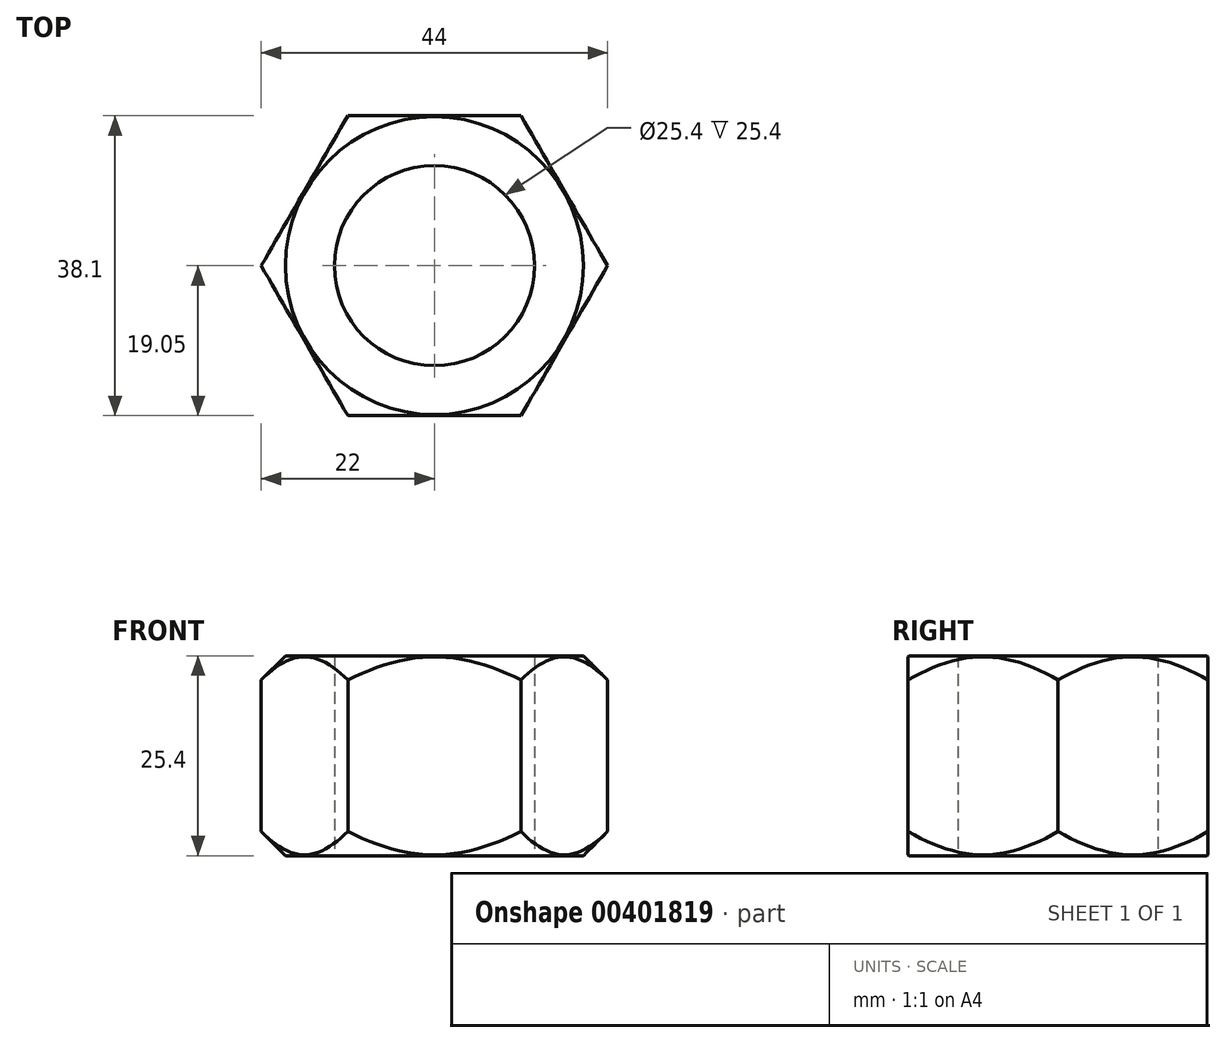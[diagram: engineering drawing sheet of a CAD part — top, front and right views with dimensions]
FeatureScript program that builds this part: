
annotation { "Feature Type Name" : "Feature", "Feature Type Description" : "" }
export const myFeature = defineFeature(function(context is Context, id is Id, definition is map)
    precondition{}
    {
        {
            var Q0;
            Q0=qCreatedBy(makeId("Top.planeOp"),FACE);
            var sketch = newSketch(context, id + "F0", { "sketchPlane" : qUnion([Q0])});
            skCircle(sketch, "E0.cCircle", {"center": v(0, 0) * mm, "radius": 19.05 * mm, "construction": true});
            skLineSegment(sketch, "E0.0", {"start": v(-11, 19.05) * mm, "end": v(11, 19.05) * mm});
            skLineSegment(sketch, "E0.1", {"start": v(11, 19.05) * mm, "end": v(22, 0) * mm});
            skLineSegment(sketch, "E0.2", {"start": v(22, 0) * mm, "end": v(11, -19.05) * mm});
            skLineSegment(sketch, "E0.3", {"start": v(11, -19.05) * mm, "end": v(-11, -19.05) * mm});
            skLineSegment(sketch, "E0.4", {"start": v(-11, -19.05) * mm, "end": v(-22, 0) * mm});
            skLineSegment(sketch, "E0.5", {"start": v(-22, 0) * mm, "end": v(-11, 19.05) * mm});
            skPoint(sketch, "E0.0.midPoint", {"position": v(0, 19.05) * mm});
            skCircle(sketch, "E1", {"center": v(0, 0) * mm, "radius": 12.7 * mm});
            skSolve(sketch);
        }
        {
            var Q0;
            Q0=makeQuery(id+"F0.imprint","IMPRINT",FACE,{"disambiguationData":[TD([[makeQuery(id+"F0.imprint","IMPRINT",EDGE,{"derivedFrom":sQuery(id+"F0.wireOp",EDGE,"E0.0")}),-1.0]])]});
            extrude(context, id + "F1", {"entities" : qUnion([Q0]), "depth" : 25.4 * mm});
        }
        {
            var Q0;
            Q0=qCreatedBy(makeId("Front.planeOp"),FACE);
            var sketch = newSketch(context, id + "F2", { "sketchPlane" : qUnion([Q0])});
            skLineSegment(sketch, "E2.bottom", {"start": v(-18.92, 0) * mm, "end": v(-22.1, 0) * mm});
            skLineSegment(sketch, "E2.top", {"start": v(-18.92, 25.4) * mm, "end": v(-22.1, 25.4) * mm});
            skLineSegment(sketch, "E2.right", {"start": v(-22.1, 0) * mm, "end": v(-22.1, 3.17) * mm});
            skLineSegment(sketch, "E3", {"start": v(-22.1, 3.18) * mm, "end": v(-18.92, 0) * mm});
            skLineSegment(sketch, "E4", {"start": v(-22.1, 22.23) * mm, "end": v(-18.92, 25.4) * mm});
            skLineSegment(sketch, "E5.trimOffspring", {"start": v(-22.1, 22.23) * mm, "end": v(-22.1, 25.4) * mm});
            skPoint(sketch, "E6.orphan", {"position": v(-15.75, 0) * mm});
            skSolve(sketch);
        }
        {
            var Q0;
            Q0 = qSketchRegion(id + "F2", true);
            var Q1;
            Q1=makeQuery(id+"F1.opExtrude","SWEPT_FACE",FACE,{"disambiguationData":[OSD([sQuery(id+"F0.wireOp",EDGE,"E1")])]});
            revolve(context, id + "F3", {"operationType" : NewBodyOperationType.REMOVE, "entities" : qUnion([Q0]), "axis" : qUnion([Q1]), "revolveType" : RevolveType.FULL, "oppositeDirection" : true});
        }
    });
